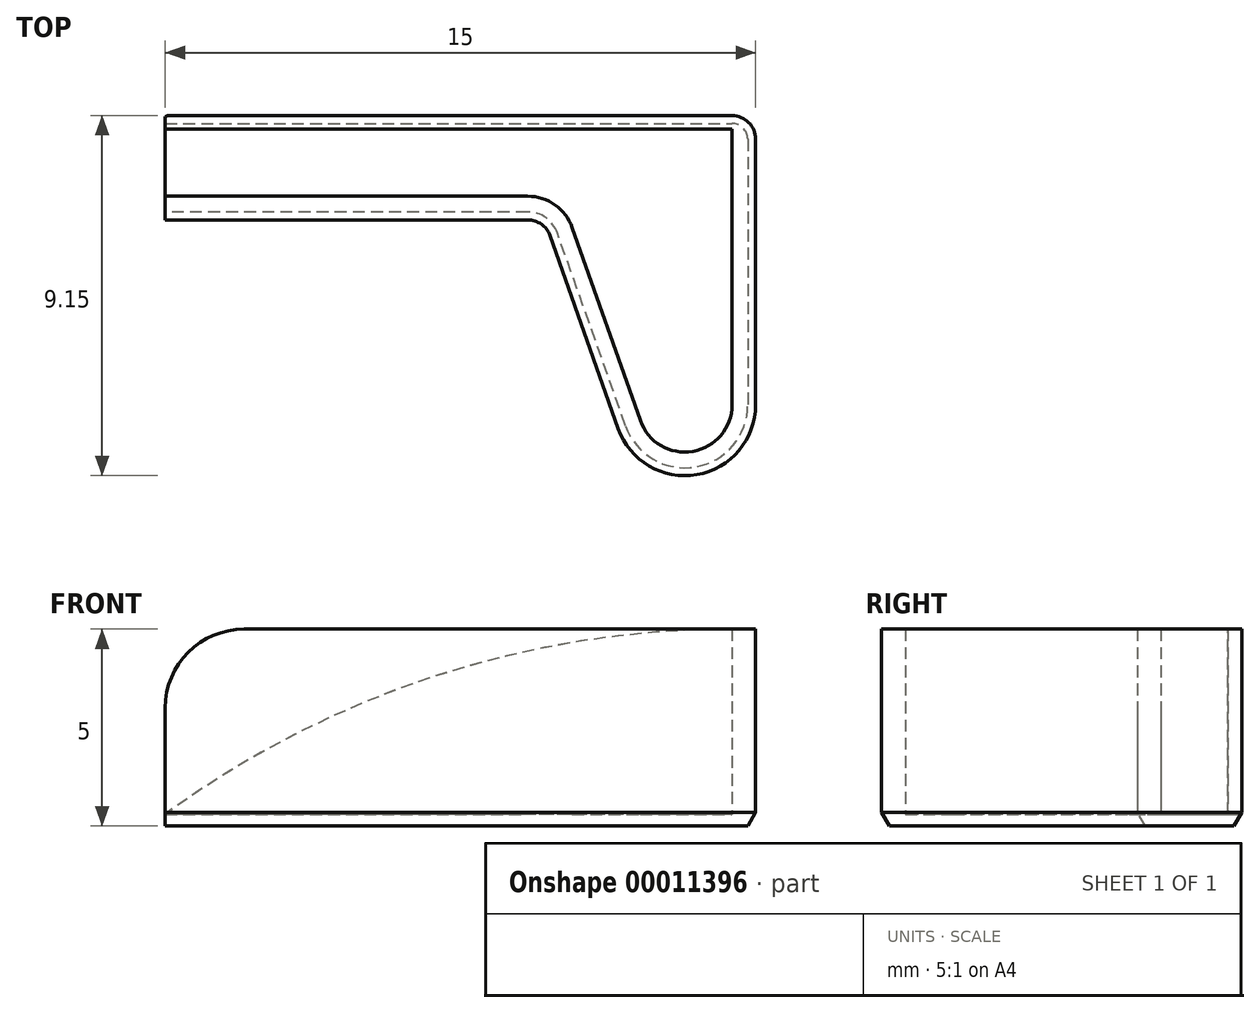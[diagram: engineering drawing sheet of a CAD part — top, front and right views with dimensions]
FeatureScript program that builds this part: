
annotation { "Feature Type Name" : "Feature", "Feature Type Description" : "" }
export const myFeature = defineFeature(function(context is Context, id is Id, definition is map)
    precondition{}
    {
        {
            var Q0;
            Q0=qCreatedBy(makeId("Top.planeOp"),FACE);
            var sketch = newSketch(context, id + "F0", { "sketchPlane" : qUnion([Q0])});
            skLineSegment(sketch, "E0", {"start": v(-14.2, 0) * mm, "end": v(0, 0) * mm});
            skLineSegment(sketch, "E1", {"start": v(0, 0) * mm, "end": v(0, -6.8) * mm});
            skArc(sketch, "E2", {"start": v(0, -6.8) * mm, "mid": v(-0.83, -7.79) * mm, "end": v(-1.94, -7.13) * mm});
            skLineSegment(sketch, "E3", {"start": v(-1.94, -7.13) * mm, "end": v(-4, -1.3) * mm});
            skLineSegment(sketch, "E4", {"start": v(-4, -1.3) * mm, "end": v(-14.2, -1.3) * mm});
            skLineSegment(sketch, "E5", {"start": v(-14.2, -1.3) * mm, "end": v(-14.2, 0) * mm});
            skLineSegment(sketch, "E6.0", {"start": v(-4.14, -1.5) * mm, "end": v(-14.2, -1.5) * mm});
            skLineSegment(sketch, "E6.1", {"start": v(-14.2, 0.2) * mm, "end": v(0.2, 0.2) * mm});
            skLineSegment(sketch, "E6.2", {"start": v(0.2, 0.2) * mm, "end": v(0.2, -6.8) * mm});
            skArc(sketch, "E6.3", {"start": v(0.2, -6.8) * mm, "mid": v(-0.8, -7.98) * mm, "end": v(-2.13, -7.2) * mm});
            skLineSegment(sketch, "E6.4", {"start": v(-2.13, -7.2) * mm, "end": v(-4.14, -1.5) * mm});
            skLineSegment(sketch, "E7.0", {"start": v(-4.57, -2.1) * mm, "end": v(-14.2, -2.1) * mm});
            skLineSegment(sketch, "E7.2", {"start": v(0.8, 0.55) * mm, "end": v(0.8, -6.8) * mm});
            skArc(sketch, "E7.3", {"start": v(0.8, -6.8) * mm, "mid": v(-0.7, -8.57) * mm, "end": v(-2.7, -7.4) * mm});
            skLineSegment(sketch, "E7.4", {"start": v(-2.7, -7.4) * mm, "end": v(-4.57, -2.1) * mm});
            skLineSegment(sketch, "E8", {"start": v(0.8, 0.55) * mm, "end": v(-14.2, 0.55) * mm});
            skLineSegment(sketch, "E9", {"start": v(-14.2, 0.2) * mm, "end": v(-14.2, 0.55) * mm});
            skLineSegment(sketch, "E10", {"start": v(-14.2, -1.5) * mm, "end": v(-14.2, -2.1) * mm});
            skLineSegment(sketch, "E11", {"start": v(-14.2, -1.5) * mm, "end": v(-14.2, -1.3) * mm});
            skLineSegment(sketch, "E12", {"start": v(-14.2, 0) * mm, "end": v(-14.2, 0.2) * mm});
            skSolve(sketch);
        }
        {
            var Q0;
            Q0=makeQuery(id+"F0.imprint","IMPRINT",FACE,{"disambiguationData":[TD([[makeQuery(id+"F0.imprint","IMPRINT",EDGE,{"derivedFrom":sQuery(id+"F0.wireOp",EDGE,"E6.0")}),1.0]])]});
            var Q1;
            Q1=makeQuery(id+"F0.imprint","IMPRINT",FACE,{"disambiguationData":[TD([[makeQuery(id+"F0.imprint","IMPRINT",EDGE,{"derivedFrom":sQuery(id+"F0.wireOp",EDGE,"E0")}),-1.0]])]});
            var Q2;
            Q2=makeQuery(id+"F0.imprint","IMPRINT",FACE,{"disambiguationData":[TD([[makeQuery(id+"F0.imprint","IMPRINT",EDGE,{"derivedFrom":sQuery(id+"F0.wireOp",EDGE,"E0")}),1.0]])]});
            extrude(context, id + "F1", {"entities" : qUnion([Q0, Q1, Q2]), "depth" : 0.3 * mm, "offsetDistance" : 25 * mm});
        }
        {
            var Q0;
            Q0=makeQuery(id+"F0.imprint","IMPRINT",FACE,{"disambiguationData":[TD([[makeQuery(id+"F0.imprint","IMPRINT",EDGE,{"derivedFrom":sQuery(id+"F0.wireOp",EDGE,"E6.0")}),1.0]])]});
            extrude(context, id + "F2", {"entities" : qUnion([Q0]), "operationType" : NewBodyOperationType.ADD, "depth" : 5 * mm, "offsetDistance" : 25 * mm});
        }
        {
            var Q0;
            {var subQ0=sQuery(id+"F0.wireOp",EDGE,"E8");Q0=makeQuery(id+"F2.boolean.opBoolean","MERGE",FACE,{"derivedFrom":[makeQuery(id+"F1.opExtrude","SWEPT_FACE",FACE,{"disambiguationData":[OSD([subQ0])]}),makeQuery(id+"F2.opExtrude","SWEPT_FACE",FACE,{"disambiguationData":[OSD([subQ0])]})]});}
            var sketch = newSketch(context, id + "F3", { "sketchPlane" : qUnion([Q0])});
            skLineSegment(sketch, "E13", {"start": v(14.2, 0.3) * mm, "end": v(17.21, 0.3) * mm});
            skLineSegment(sketch, "E14", {"start": v(17.21, 0.3) * mm, "end": v(17.21, 8.56) * mm});
            skLineSegment(sketch, "E15", {"start": v(17.21, 8.56) * mm, "end": v(-0.2, 8.56) * mm});
            skLineSegment(sketch, "E16", {"start": v(-0.2, 8.56) * mm, "end": v(-0.2, 5) * mm});
            skArc(sketch, "E17", {"start": v(14.2, 0.3) * mm, "mid": v(7.37, 3.8) * mm, "end": v(-0.2, 5) * mm});
            skSolve(sketch);
        }
        {
            var Q0;
            Q0 = qSketchRegion(id + "F3", true);
            var Q1;
            Q1=makeQuery(id+"F2.opExtrude","SWEPT_FACE",FACE,{"disambiguationData":[OSD([sQuery(id+"F0.wireOp",EDGE,"E6.1")])]});
            extrude(context, id + "F4", {"entities" : qUnion([Q0]), "operationType" : NewBodyOperationType.REMOVE, "endBound" : BoundingType.UP_TO_SURFACE, "oppositeDirection" : true, "depth" : 25 * mm, "endBoundEntityFace" : qUnion([Q1]), "offsetDistance" : 25 * mm});
        }
        {
            var Q0;
            Q0=makeQuery(id+"F2.opExtrude","CAP_EDGE",EDGE,{"disambiguationData":[OSD([sQuery(id+"F0.wireOp",EDGE,"E10")])],"isStart":false});
            fillet(context, id + "F5", {"entities" : qUnion([Q0]), "radius" : 2 * mm, "tangentPropagation" : true, "allowEdgeOverflow" : false});
        }
        {
            var Q0;
            {var subQ0=sQuery(id+"F0.wireOp",EDGE,"E8");var subQ1=sQuery(id+"F0.wireOp",EDGE,"E7.2");Q0=makeQuery(id+"F2.boolean.opBoolean","MERGE",EDGE,{"derivedFrom":[makeQuery(id+"F1.opExtrude","SWEPT_EDGE",EDGE,{"disambiguationData":[OSD([subQ1,subQ0])]}),makeQuery(id+"F2.opExtrude","SWEPT_EDGE",EDGE,{"disambiguationData":[OSD([subQ1,subQ0])]})]});}
            var Q1;
            {var subQ0=sQuery(id+"F0.wireOp",EDGE,"E7.4");var subQ1=sQuery(id+"F0.wireOp",EDGE,"E7.0");Q1=makeQuery(id+"F2.boolean.opBoolean","MERGE",EDGE,{"derivedFrom":[makeQuery(id+"F1.opExtrude","SWEPT_EDGE",EDGE,{"disambiguationData":[OSD([subQ1,subQ0])]}),makeQuery(id+"F2.opExtrude","SWEPT_EDGE",EDGE,{"disambiguationData":[OSD([subQ1,subQ0])]})]});}
            fillet(context, id + "F6", {"entities" : qUnion([Q0, Q1]), "radius" : 0.6 * mm, "tangentPropagation" : true, "allowEdgeOverflow" : false});
        }
        {
            var Q0;
            Q0=makeQuery(id+"F2.opExtrude","SWEPT_EDGE",EDGE,{"disambiguationData":[OSD([sQuery(id+"F0.wireOp",EDGE,"E6.0"),sQuery(id+"F0.wireOp",EDGE,"E6.4")])]});
            fillet(context, id + "F7", {"entities" : qUnion([Q0]), "radius" : 1.2 * mm, "tangentPropagation" : true, "allowEdgeOverflow" : false});
        }
        {
            var Q0;
            Q0=makeQuery(id+"F1.opExtrude","CAP_EDGE",EDGE,{"disambiguationData":[OSD([sQuery(id+"F0.wireOp",EDGE,"E7.0")])],"isStart":true});
            chamfer(context, id + "F8", {"entities" : qUnion([Q0]), "chamferType" : ChamferType.OFFSET_ANGLE, "width" : 0.2 * mm, "oppositeDirection" : false, "angle" : 60 * degree, "tangentPropagation" : true});
        }
    });
